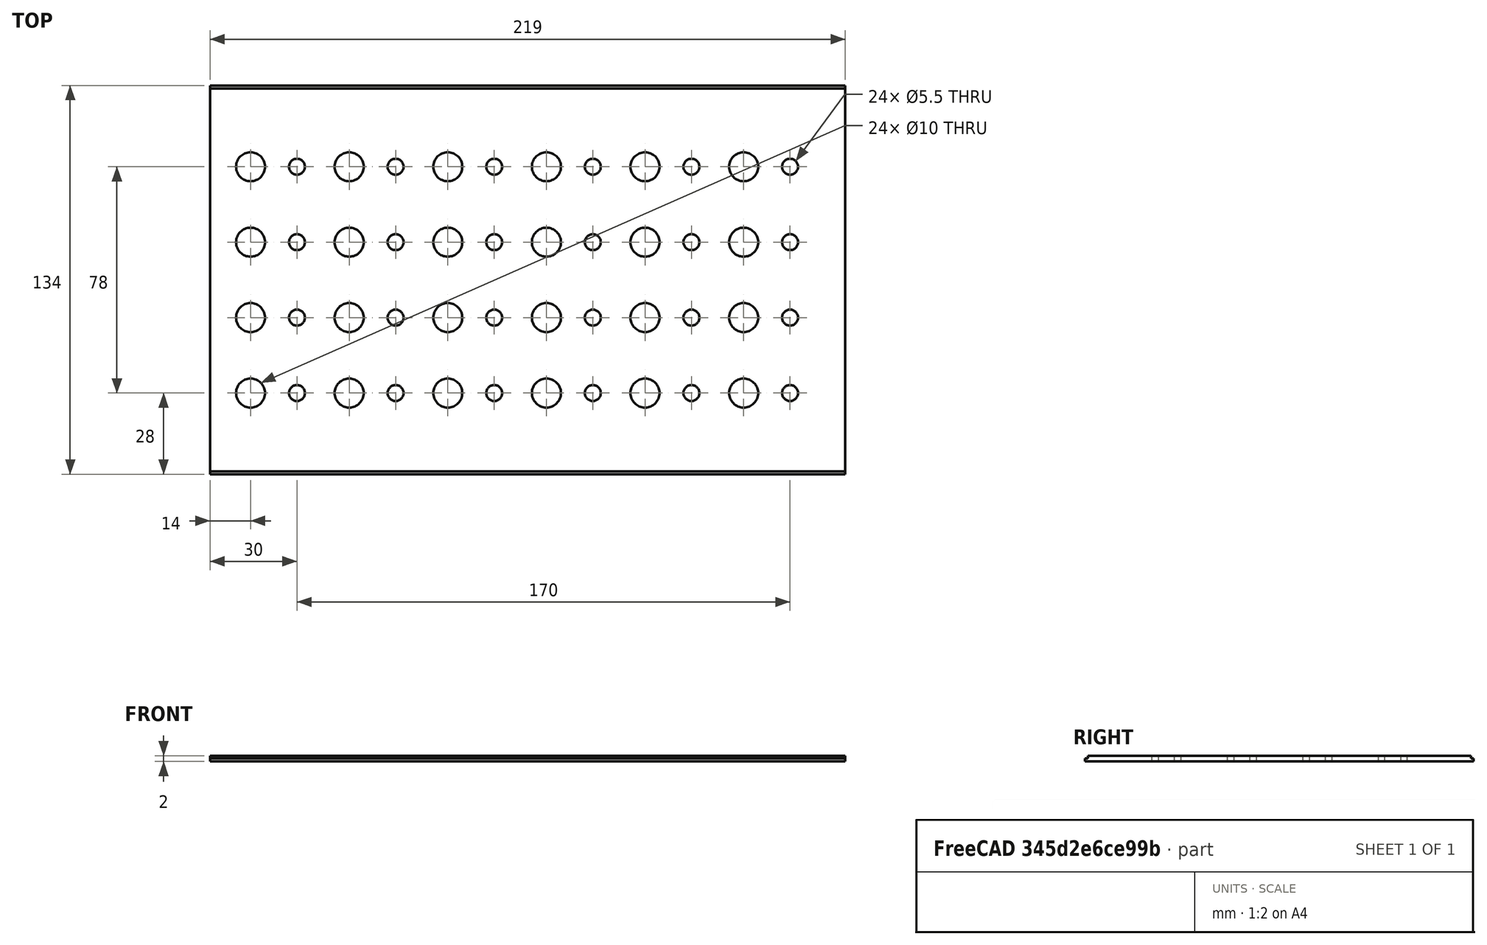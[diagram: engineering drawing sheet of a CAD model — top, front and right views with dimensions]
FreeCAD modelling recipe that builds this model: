
FCSTD DOCUMENT  (FreeCAD 0.18.4R)
Label: 顶板
License: All rights reserved
LicenseURL: http://en.wikipedia.org/wiki/All_rights_reserved
objects: TechDraw::DrawViewDimension×9, Sketcher::SketchObject×3, PartDesign::Pocket×2, PartDesign::Pad×1, PartDesign::LinearPattern×1, PartDesign::Mirrored×1, PartDesign::Body×1, TechDraw::DrawSVGTemplate×1, TechDraw::DrawViewPart×1, TechDraw::DrawPage×1
note: 12 computed .brp shape members not serialized (recipe doc carries the construction recipe); baked Part::Feature solids carry a one-line shape summary decoded from their .brp

FEATURE [Sketcher::SketchObject] Sketch
  MapMode = 2
  Support = -> [Sketch]
  sketch-geometry (4):
    g0: LineSegment StartX=-109.5 StartY=67 StartZ=0 EndX=109.5 EndY=67 EndZ=0
    g1: LineSegment StartX=109.5 StartY=67 StartZ=0 EndX=109.5 EndY=-67 EndZ=0
    g2: LineSegment StartX=109.5 StartY=-67 StartZ=0 EndX=-109.5 EndY=-67 EndZ=0
    g3: LineSegment StartX=-109.5 StartY=-67 StartZ=0 EndX=-109.5 EndY=67 EndZ=0
  constraints (11):
    c: Coincident(g0,g1)
    c: Coincident(g1,g2)
    c: Coincident(g2,g3)
    c: Coincident(g3,g0)
    c: Horizontal(g0)
    c: Horizontal(g2)
    c: Vertical(g1)
    c: Vertical(g3)
    c: DistanceX(g0,g0) = 219
    c: DistanceY(g1,g1) = 134
    c: Symmetric(g0,g1,g-1)
FEATURE [PartDesign::Pad] Pad
  Length = 2
  Length2 = 100
  Profile = -> Sketch
  Type = 0
FEATURE [Sketcher::SketchObject] Sketch001
  ExternalGeometry = -> [Pad]
  MapMode = 5
  Support = -> [XY_Plane]
  sketch-geometry (12):
    g0: Circle CenterX=-95.5 CenterY=39 CenterZ=0 NormalX=0 NormalY=0 NormalZ=1 AngleXU=0 Radius=5
    g1: Circle CenterX=-95.5 CenterY=13 CenterZ=0 NormalX=0 NormalY=0 NormalZ=1 AngleXU=0 Radius=5
    g2: Circle CenterX=-95.5 CenterY=-13 CenterZ=0 NormalX=0 NormalY=0 NormalZ=1 AngleXU=0 Radius=5
    g3: Circle CenterX=-95.5 CenterY=-39 CenterZ=0 NormalX=0 NormalY=0 NormalZ=1 AngleXU=0 Radius=5
    g4: Circle CenterX=-79.5 CenterY=39 CenterZ=0 NormalX=0 NormalY=0 NormalZ=1 AngleXU=0 Radius=2.75
    g5: Circle CenterX=-79.5 CenterY=13 CenterZ=0 NormalX=0 NormalY=0 NormalZ=1 AngleXU=0 Radius=2.75
    g6: Circle CenterX=-79.5 CenterY=-13 CenterZ=0 NormalX=0 NormalY=0 NormalZ=1 AngleXU=0 Radius=2.75
    g7: Circle CenterX=-79.5 CenterY=-39 CenterZ=0 NormalX=0 NormalY=0 NormalZ=1 AngleXU=0 Radius=2.75
    g8: LineSegment [constr] StartX=-95.5 StartY=39 StartZ=0 EndX=-95.5 EndY=-39 EndZ=0
    g9: LineSegment [constr] StartX=-95.5 StartY=0.063638 StartZ=0 EndX=-109.5 EndY=0.063638 EndZ=0
    g10: LineSegment [constr] StartX=-79.5 StartY=39 StartZ=0 EndX=-79.5 EndY=-39 EndZ=0
    g11: LineSegment [constr] StartX=-95.5 StartY=-0.095093 StartZ=0 EndX=-79.5 EndY=-0.095093 EndZ=0
  constraints (34):
    c: Vertical(g8)
    c: PointOnObject(g1,g8)
    c: PointOnObject(g2,g8)
    c: Coincident(g3,g8)
    c: Diameter(g0) = 10
    c: Diameter(g1) = 10
    c: Diameter(g2) = 10
    c: Diameter(g3) = 10
    c: PointOnObject(g9,g-3)
    c: PointOnObject(g9,g8)
    c: Horizontal(g9)
    c: DistanceX(g9,g9) = 14
    c: DistanceY(g1) = 13
    c: DistanceY(g0) = 39
    c: DistanceY(g2) = -13
    c: DistanceY(g3) = -39
    c: Diameter(g4) = 5.5
    c: Diameter(g5) = 5.5
    c: Diameter(g6) = 5.5
    c: Diameter(g7) = 5.5
    c: PointOnObject(g5,g10)
    c: PointOnObject(g6,g10)
    c: Coincident(g10,g7)
    c: Vertical(g10)
    c: PointOnObject(g11,g10)
    c: PointOnObject(g11,g8)
    c: Horizontal(g11)
    c: DistanceX(g11,g11) = 16
    c: Coincident(g4,g10)
    c: DistanceY(g5) = 13
    c: DistanceY(g4) = 39
    c: Coincident(g0,g8)
    c: DistanceY(g6) = -13
    c: DistanceY(g7) = -39
FEATURE [PartDesign::Pocket] Pocket
  BaseFeature = -> Pad
  Length = 5
  Length2 = 100
  Profile = -> Sketch001
  Reversed = true
  Type = 1
FEATURE [PartDesign::LinearPattern] LinearPattern
  BaseFeature = -> Pocket
  Direction = -> Sketch001 [H_Axis]
  Length = 170
  Occurrences = 6
  Originals = -> [Pocket]
FEATURE [Sketcher::SketchObject] Sketch002
  ExternalGeometry = -> [LinearPattern]
  MapMode = 5
  Placement = pos=(0,0,2) rot=(0,0,1;0rad)
  Support = -> [LinearPattern]
  sketch-geometry (4):
    g0: LineSegment StartX=-109.5 StartY=67 StartZ=0 EndX=109.5 EndY=67 EndZ=0
    g1: LineSegment StartX=109.5 StartY=67 StartZ=0 EndX=109.5 EndY=66 EndZ=0
    g2: LineSegment StartX=109.5 StartY=66 StartZ=0 EndX=-109.5 EndY=66 EndZ=0
    g3: LineSegment StartX=-109.5 StartY=66 StartZ=0 EndX=-109.5 EndY=67 EndZ=0
  constraints (10):
    c: Coincident(g0,g1)
    c: Coincident(g1,g2)
    c: Coincident(g2,g3)
    c: Coincident(g3,g0)
    c: Horizontal(g2)
    c: Vertical(g1)
    c: Vertical(g3)
    c: Coincident(g0,g-5)
    c: DistanceY(g1,g1) = 1
    c: Coincident(g0,g-4)
FEATURE [PartDesign::Pocket] Pocket001
  BaseFeature = -> LinearPattern
  Length = 1
  Length2 = 100
  Profile = -> Sketch002
  Type = 0
FEATURE [PartDesign::Mirrored] Mirrored
  BaseFeature = -> Pocket001
  MirrorPlane = -> XZ_Plane
  Originals = -> [Pocket001]
FEATURE [PartDesign::Body] Body
  Group = -> [Sketch,Pad,Sketch001,Pocket,LinearPattern,Sketch002,Pocket001,Mirrored]
  Origin = -> Origin
  Tip = -> Mirrored
FEATURE [TechDraw::DrawSVGTemplate] Template
  EditableTexts = Designed_by_Name=岳晓凯; FC-Date=2020/11/15; FC-Title=Title; Subtitle=接线盒顶板
  Height = 210
  Orientation = 1
  Width = 297
FEATURE [TechDraw::DrawViewPart] View
  CoarseView = false
  Direction = (0,0,1)
  Focus = 100
  HardHidden = false
  IsoCount = 0
  IsoHidden = false
  IsoVisible = false
  LockPosition = false
  Perspective = false
  Rotation = 0
  Scale = 0.8
  ScaleType = 0
  SeamHidden = false
  SeamVisible = false
  SmoothHidden = false
  SmoothVisible = false
  Source = -> [Body]
  X = 141.908
  Y = 130.426
FEATURE [TechDraw::DrawViewDimension] Dimension
  Arbitrary = false
  FormatSpec = ⌀%.2f
  LockPosition = false
  MeasureType = 1
  OverTolerance = 0
  References2D = -> [View]
  Rotation = 0
  ScaleType = 0
  Type = 5
  UnderTolerance = 0
  X = -57.2085
  Y = 45.6726
FEATURE [TechDraw::DrawViewDimension] Dimension001
  Arbitrary = false
  FormatSpec = ⌀%.2f
  LockPosition = false
  MeasureType = 1
  OverTolerance = 0
  References2D = -> [View]
  Rotation = 0
  ScaleType = 0
  Type = 5
  UnderTolerance = 0
  X = -44.2601
  Y = 22.6009
FEATURE [TechDraw::DrawViewDimension] Dimension002
  Arbitrary = false
  FormatSpec = %.2f
  LockPosition = false
  MeasureType = 1
  OverTolerance = 0
  References2D = -> [View]
  Rotation = 0
  ScaleType = 0
  Type = 1
  UnderTolerance = 0
  X = -65.3133
  Y = -44.8242
FEATURE [TechDraw::DrawViewDimension] Dimension003
  Arbitrary = false
  FormatSpec = %.2f
  LockPosition = false
  MeasureType = 1
  OverTolerance = 0
  References2D = -> [View]
  Rotation = 0
  ScaleType = 0
  Type = 1
  UnderTolerance = 0
  X = -61.0289
  Y = -19.6194
FEATURE [TechDraw::DrawViewDimension] Dimension004
  Arbitrary = false
  FormatSpec = %.2f
  LockPosition = false
  MeasureType = 1
  OverTolerance = 0
  References2D = -> [View]
  Rotation = 0
  ScaleType = 0
  Type = 2
  UnderTolerance = 0
  X = -94.7927
  Y = 1.22618
FEATURE [TechDraw::DrawViewDimension] Dimension005
  Arbitrary = false
  FormatSpec = %.2f
  LockPosition = false
  MeasureType = 1
  OverTolerance = 0
  References2D = -> [View]
  Rotation = 0
  ScaleType = 0
  Type = 2
  UnderTolerance = 0
  X = -84.9015
  Y = 20.8
FEATURE [TechDraw::DrawViewDimension] Dimension006
  Arbitrary = false
  FormatSpec = %.2f
  LockPosition = false
  MeasureType = 1
  OverTolerance = 0
  References2D = -> [View]
  Rotation = 0
  ScaleType = 0
  Type = 2
  UnderTolerance = 0
  X = -97.9807
  Y = -21.454
FEATURE [TechDraw::DrawViewDimension] Dimension007
  Arbitrary = false
  FormatSpec = %.2f
  LockPosition = false
  MeasureType = 1
  OverTolerance = 0
  References2D = -> [View]
  Rotation = 0
  ScaleType = 0
  Type = 1
  UnderTolerance = 0
  X = -77.7493
  Y = -37.5761
FEATURE [TechDraw::DrawViewDimension] Dimension008
  Arbitrary = false
  FormatSpec = %.2f
  LockPosition = false
  MeasureType = 1
  OverTolerance = 0
  References2D = -> [View]
  Rotation = 0
  ScaleType = 0
  Type = 1
  UnderTolerance = 0
  X = 0.53494
  Y = -61.9812
FEATURE [TechDraw::DrawPage] Page
  KeepUpdated = true
  ProjectionType = 0
  Template = -> Template
  Views = -> [View,Dimension,Dimension001,Dimension002,Dimension003,Dimension004,Dimension005,Dimension006,Dimension007,Dimension008]
